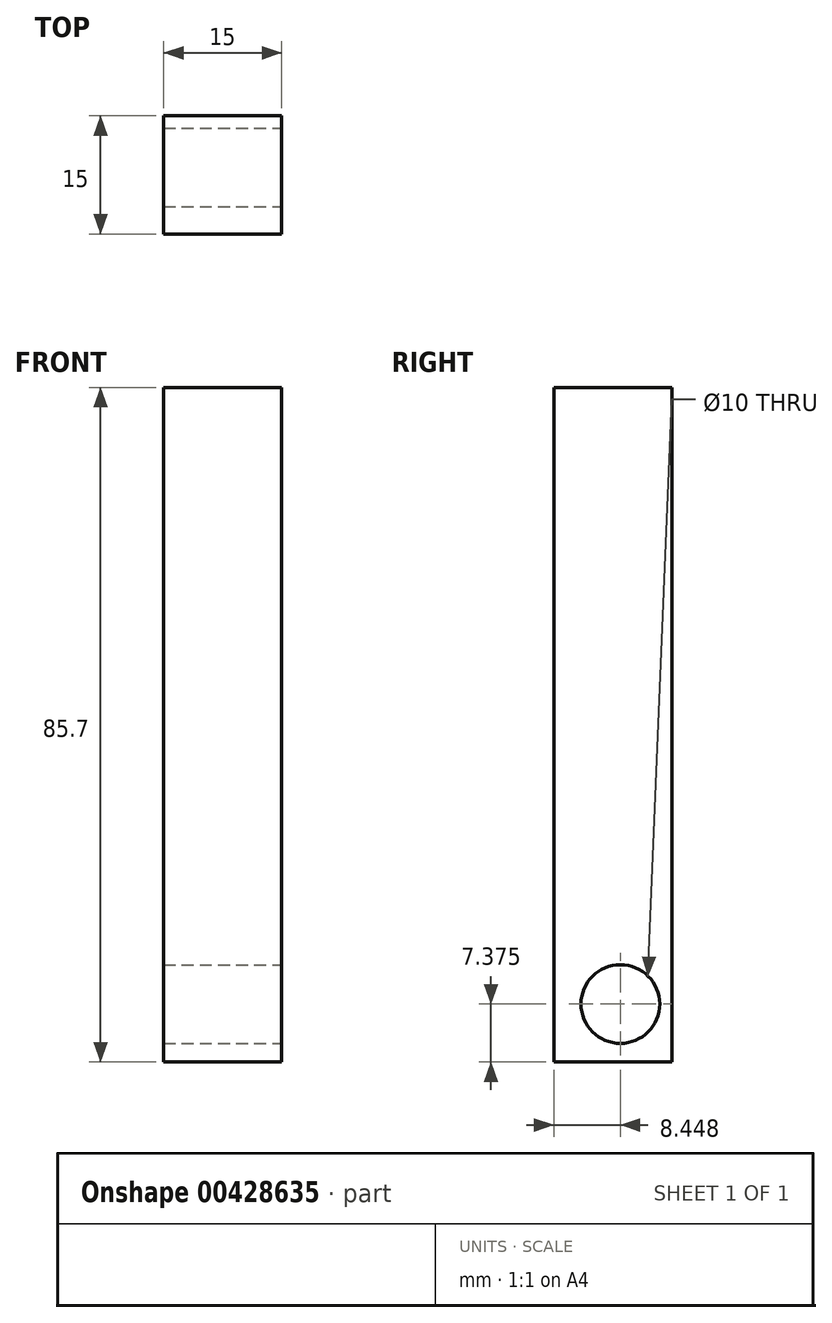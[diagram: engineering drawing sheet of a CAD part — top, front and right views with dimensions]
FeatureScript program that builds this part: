
annotation { "Feature Type Name" : "Feature", "Feature Type Description" : "" }
export const myFeature = defineFeature(function(context is Context, id is Id, definition is map)
    precondition{}
    {
        {
            var Q0;
            Q0=qCreatedBy(makeId("Top.planeOp"),FACE);
            var sketch = newSketch(context, id + "F0", { "sketchPlane" : qUnion([Q0])});
            skLineSegment(sketch, "E0.bottom", {"start": v(0, 0) * mm, "end": v(-15, 0) * mm});
            skLineSegment(sketch, "E0.top", {"start": v(0, 15) * mm, "end": v(-15, 15) * mm});
            skLineSegment(sketch, "E0.left", {"start": v(0, 0) * mm, "end": v(0, 15) * mm});
            skLineSegment(sketch, "E0.right", {"start": v(-15, 0) * mm, "end": v(-15, 15) * mm});
            skSolve(sketch);
        }
        {
            var Q0;
            Q0 = qSketchRegion(id + "F0", true);
            extrude(context, id + "F1", {"entities" : qUnion([Q0]), "depth" : 85.7 * mm});
        }
        {
            var Q0;
            Q0=makeQuery(id+"F1.opExtrude","SWEPT_FACE",FACE,{"disambiguationData":[OSD([sQuery(id+"F0.wireOp",EDGE,"E0.left")])]});
            var sketch = newSketch(context, id + "F2", { "sketchPlane" : qUnion([Q0])});
            skCircle(sketch, "E1", {"center": v(8.45, 7.38) * mm, "radius": 5 * mm});
            skSolve(sketch);
        }
        {
            var Q0;
            Q0=makeQuery(id+"F2.imprint","IMPRINT",FACE,{"disambiguationData":[TD([[makeQuery(id+"F2.imprint","IMPRINT",EDGE,{"derivedFrom":sQuery(id+"F2.wireOp",EDGE,"E1")}),1.0]])]});
            extrude(context, id + "F3", {"entities" : qUnion([Q0]), "operationType" : NewBodyOperationType.REMOVE, "endBound" : BoundingType.THROUGH_ALL, "oppositeDirection" : true, "depth" : 25 * mm});
        }
    });
